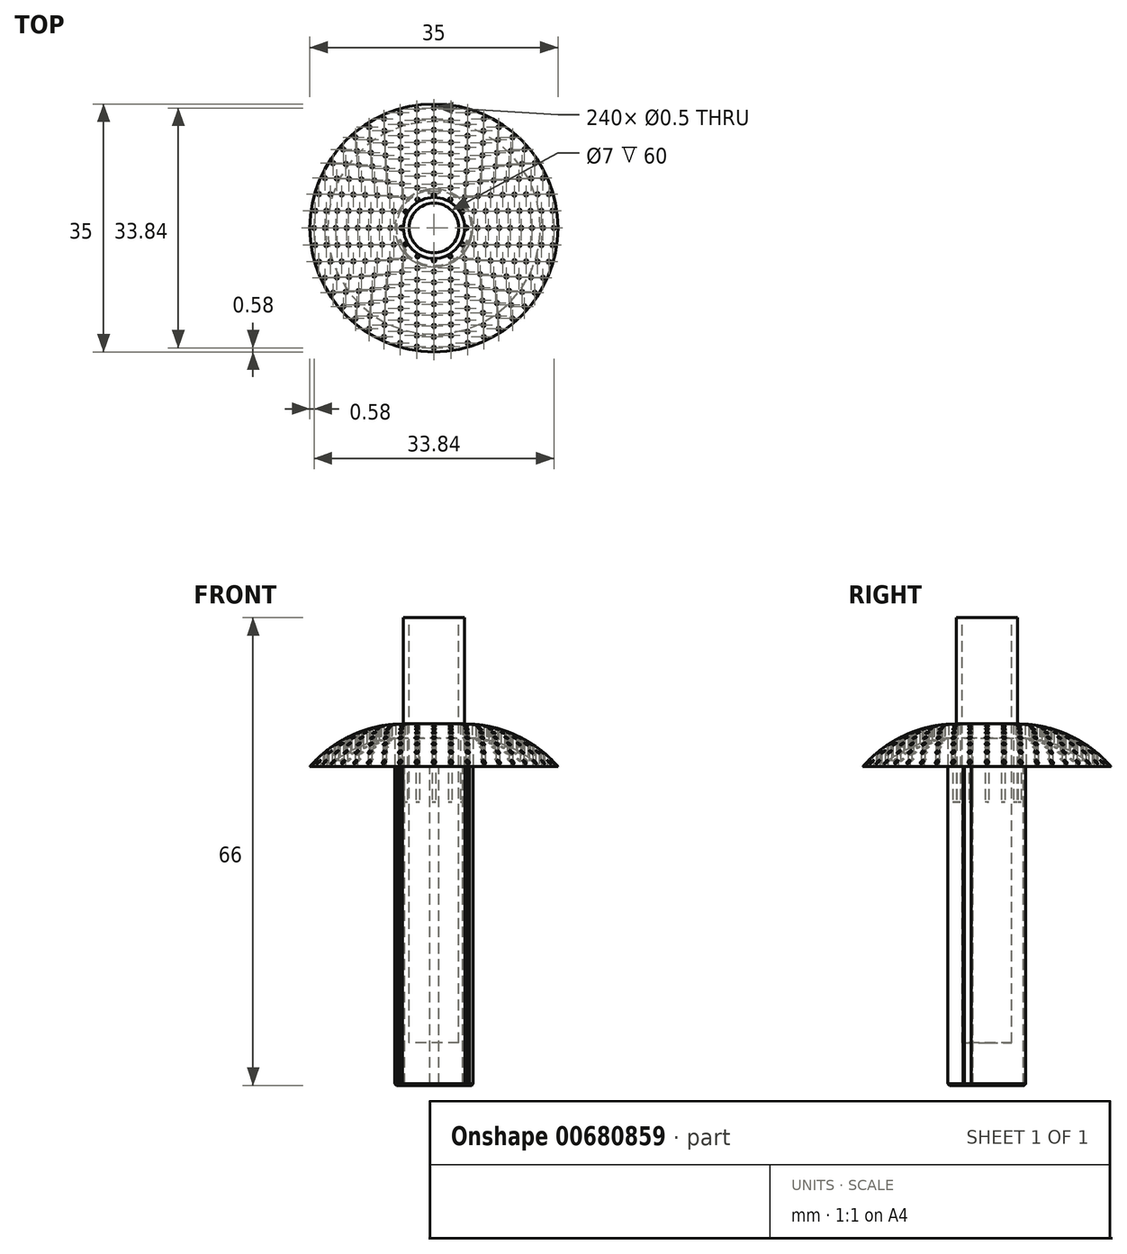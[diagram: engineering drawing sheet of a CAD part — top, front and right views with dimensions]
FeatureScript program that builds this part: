
annotation { "Feature Type Name" : "Feature", "Feature Type Description" : "" }
export const myFeature = defineFeature(function(context is Context, id is Id, definition is map)
    precondition{}
    {
        {
            var Q0;
            Q0=qCreatedBy(makeId("Top.planeOp"),FACE);
            var sketch = newSketch(context, id + "F0", { "sketchPlane" : qUnion([Q0])});
            skCircle(sketch, "E0", {"center": v(0, 0) * mm, "radius": 5.5 * mm});
            skSolve(sketch);
        }
        {
            var Q0;
            Q0=makeQuery(id+"F0.imprint","IMPRINT",FACE,{"disambiguationData":[TD([[makeQuery(id+"F0.imprint","IMPRINT",EDGE,{"derivedFrom":sQuery(id+"F0.wireOp",EDGE,"E0")}),1.0]])]});
            var Q1;
            Q1=sQuery(id+"F0.wireOp",EDGE,"E0");
            extrude(context, id + "F1", {"entities" : qUnion([Q0]), "surfaceEntities" : qUnion([Q1]), "depth" : 45 * mm, "offsetDistance" : 25 * mm});
        }
        {
            var Q0;
            Q0=makeQuery(id+"F1.opExtrude","CAP_FACE",FACE,{"disambiguationData":[OSD([sQuery(id+"F0.wireOp",EDGE,"E0")])],"isStart":false});
            var sketch = newSketch(context, id + "F2", { "sketchPlane" : qUnion([Q0])});
            skLineSegment(sketch, "E1.bottom", {"start": v(-0.6, 7.22) * mm, "end": v(0.71, 7.22) * mm});
            skLineSegment(sketch, "E1.top", {"start": v(-0.6, 5.12) * mm, "end": v(0.71, 5.12) * mm});
            skLineSegment(sketch, "E1.left", {"start": v(-0.6, 7.22) * mm, "end": v(-0.6, 5.12) * mm});
            skLineSegment(sketch, "E1.right", {"start": v(0.71, 7.22) * mm, "end": v(0.71, 5.12) * mm});
            skLineSegment(sketch, "E2.1.0", {"start": v(-6.6, -2.99) * mm, "end": v(-4.8, -1.94) * mm});
            skLineSegment(sketch, "E2.1.1", {"start": v(-4.13, -3.08) * mm, "end": v(-4.8, -1.94) * mm});
            skLineSegment(sketch, "E2.1.2", {"start": v(-5.95, -4.13) * mm, "end": v(-4.13, -3.08) * mm});
            skLineSegment(sketch, "E2.1.3", {"start": v(-5.95, -4.13) * mm, "end": v(-6.6, -2.99) * mm});
            skLineSegment(sketch, "E2.2.0", {"start": v(5.9, -4.23) * mm, "end": v(4.08, -3.18) * mm});
            skLineSegment(sketch, "E2.2.1", {"start": v(4.73, -2.04) * mm, "end": v(4.08, -3.18) * mm});
            skLineSegment(sketch, "E2.2.2", {"start": v(6.55, -3.09) * mm, "end": v(4.73, -2.04) * mm});
            skLineSegment(sketch, "E2.2.3", {"start": v(6.55, -3.09) * mm, "end": v(5.9, -4.23) * mm});
            skPoint(sketch, "E2.center", {"position": v(0, 0) * mm});
            skSolve(sketch);
        }
        {
            var Q0;
            Q0 = qSketchRegion(id + "F2", true);
            extrude(context, id + "F3", {"entities" : qUnion([Q0]), "operationType" : NewBodyOperationType.REMOVE, "oppositeDirection" : true, "depth" : 50 * mm, "offsetDistance" : 25 * mm});
        }
        {
            var Q0;
            Q0=makeQuery(id+"F1.opExtrude","CAP_FACE",FACE,{"disambiguationData":[OSD([sQuery(id+"F0.wireOp",EDGE,"E0")])],"isStart":false});
            var sketch = newSketch(context, id + "F4", { "sketchPlane" : qUnion([Q0])});
            skCircle(sketch, "E3", {"center": v(0, 0) * mm, "radius": 17.5 * mm});
            skSolve(sketch);
        }
        {
            var Q0;
            Q0 = qSketchRegion(id + "F4", true);
            extrude(context, id + "F5", {"entities" : qUnion([Q0]), "operationType" : NewBodyOperationType.ADD, "depth" : 6 * mm, "offsetDistance" : 25 * mm});
        }
        {
            var Q0;
            Q0=makeQuery(id+"F5.opExtrude","CAP_EDGE",EDGE,{"disambiguationData":[OSD([sQuery(id+"F4.wireOp",EDGE,"E3")])],"isStart":false});
            fillet(context, id + "F6", {"entities" : qUnion([Q0]), "radius" : 17.5 * mm, "tangentPropagation" : true, "allowEdgeOverflow" : false});
        }
        {
            var Q0;
            Q0=makeQuery(id+"F5.opExtrude","CAP_FACE",FACE,{"disambiguationData":[OSD([sQuery(id+"F4.wireOp",EDGE,"E3")])],"isStart":false});
            var sketch = newSketch(context, id + "F7", { "sketchPlane" : qUnion([Q0])});
            skCircle(sketch, "E4", {"center": v(0, 0) * mm, "radius": 3.5 * mm});
            skSolve(sketch);
        }
        {
            var Q0;
            Q0 = qSketchRegion(id + "F7", true);
            extrude(context, id + "F8", {"entities" : qUnion([Q0]), "operationType" : NewBodyOperationType.REMOVE, "oppositeDirection" : true, "depth" : 45 * mm, "offsetDistance" : 25 * mm});
        }
        {
            var Q0;
            Q0=makeQuery(id+"F3.boolean.opBoolean","INTERSECT",EDGE,{"derivedFrom":[makeQuery(id+"F1.opExtrude","CAP_FACE",FACE,{"disambiguationData":[OSD([sQuery(id+"F0.wireOp",EDGE,"E0")])],"isStart":true}),makeQuery(id+"F3.opExtrude","SWEPT_FACE",FACE,{"disambiguationData":[OSD([sQuery(id+"F2.wireOp",EDGE,"E2.2.1")])]})]});
            var Q1;
            Q1=makeQuery(id+"F1.opExtrude","CAP_FACE",FACE,{"disambiguationData":[OSD([sQuery(id+"F0.wireOp",EDGE,"E0")])],"isStart":true});
            chamfer(context, id + "F9", {"entities" : qUnion([Q0, Q1]), "width" : 0.2 * mm, "tangentPropagation" : true});
        }
        {
            var Q0;
            Q0=qCreatedBy(makeId("Top.planeOp"),FACE);
            cPlane(context, id + "F10", {"entities" : qUnion([Q0]), "cplaneType" : CPlaneType.OFFSET, "offset" : 40 * mm, "width" : 150 * mm, "height" : 150 * mm});
        }
        {
            var Q0;
            Q0=qCreatedBy(id+"F10.planeOp",FACE);
            var sketch = newSketch(context, id + "F11", { "sketchPlane" : qUnion([Q0])});
            skCircle(sketch, "E5", {"center": v(0, 4.6) * mm, "radius": 0.25 * mm});
            skLineSegment(sketch, "E6", {"start": v(0, 0) * mm, "end": v(0, 6.89) * mm});
            skCircle(sketch, "E7.1.0.0", {"center": v(0, 6.14) * mm, "radius": 0.25 * mm});
            skCircle(sketch, "E7.2.0.0", {"center": v(0, 7.68) * mm, "radius": 0.25 * mm});
            skCircle(sketch, "E7.3.0.0", {"center": v(0, 9.22) * mm, "radius": 0.25 * mm});
            skCircle(sketch, "E7.4.0.0", {"center": v(0, 10.76) * mm, "radius": 0.25 * mm});
            skCircle(sketch, "E7.5.0.0", {"center": v(0, 12.3) * mm, "radius": 0.25 * mm});
            skLineSegment(sketch, "E7.direction1", {"start": v(0, 4.6) * mm, "end": v(0, 6.14) * mm, "construction": true});
            skCircle(sketch, "E8.1.0", {"center": v(-2.3, 3.98) * mm, "radius": 0.25 * mm});
            skCircle(sketch, "E8.2.0", {"center": v(-3.98, 2.3) * mm, "radius": 0.25 * mm});
            skCircle(sketch, "E8.3.0", {"center": v(-4.6, 0) * mm, "radius": 0.25 * mm});
            skCircle(sketch, "E8.4.0", {"center": v(-3.98, -2.3) * mm, "radius": 0.25 * mm});
            skCircle(sketch, "E8.5.0", {"center": v(-2.3, -3.98) * mm, "radius": 0.25 * mm});
            skCircle(sketch, "E8.6.0", {"center": v(0, -4.6) * mm, "radius": 0.25 * mm});
            skCircle(sketch, "E8.7.0", {"center": v(2.3, -3.98) * mm, "radius": 0.25 * mm});
            skCircle(sketch, "E8.8.0", {"center": v(3.98, -2.3) * mm, "radius": 0.25 * mm});
            skCircle(sketch, "E8.9.0", {"center": v(4.6, 0) * mm, "radius": 0.25 * mm});
            skCircle(sketch, "E8.10.0", {"center": v(3.98, 2.3) * mm, "radius": 0.25 * mm});
            skCircle(sketch, "E8.11.0", {"center": v(2.3, 3.98) * mm, "radius": 0.25 * mm});
            skPoint(sketch, "E8.center", {"position": v(0, 0) * mm});
            skCircle(sketch, "E9.1.0", {"center": v(-2.35, 5.67) * mm, "radius": 0.25 * mm});
            skCircle(sketch, "E9.2.0", {"center": v(-4.34, 4.34) * mm, "radius": 0.25 * mm});
            skCircle(sketch, "E9.3.0", {"center": v(-5.67, 2.35) * mm, "radius": 0.25 * mm});
            skCircle(sketch, "E9.4.0", {"center": v(-6.14, 0) * mm, "radius": 0.25 * mm});
            skCircle(sketch, "E9.5.0", {"center": v(-5.67, -2.35) * mm, "radius": 0.25 * mm});
            skCircle(sketch, "E9.6.0", {"center": v(-4.34, -4.34) * mm, "radius": 0.25 * mm});
            skCircle(sketch, "E9.7.0", {"center": v(-2.35, -5.67) * mm, "radius": 0.25 * mm});
            skCircle(sketch, "E9.8.0", {"center": v(0, -6.14) * mm, "radius": 0.25 * mm});
            skCircle(sketch, "E9.9.0", {"center": v(2.35, -5.67) * mm, "radius": 0.25 * mm});
            skCircle(sketch, "E9.10.0", {"center": v(4.34, -4.34) * mm, "radius": 0.25 * mm});
            skCircle(sketch, "E9.11.0", {"center": v(5.67, -2.35) * mm, "radius": 0.25 * mm});
            skCircle(sketch, "E9.12.0", {"center": v(6.14, 0) * mm, "radius": 0.25 * mm});
            skCircle(sketch, "E9.13.0", {"center": v(5.67, 2.35) * mm, "radius": 0.25 * mm});
            skCircle(sketch, "E9.14.0", {"center": v(4.34, 4.34) * mm, "radius": 0.25 * mm});
            skCircle(sketch, "E9.15.0", {"center": v(2.35, 5.67) * mm, "radius": 0.25 * mm});
            skCircle(sketch, "E10.1.0", {"center": v(-2.37, 7.3) * mm, "radius": 0.25 * mm});
            skCircle(sketch, "E10.2.0", {"center": v(-4.51, 6.21) * mm, "radius": 0.25 * mm});
            skCircle(sketch, "E10.3.0", {"center": v(-6.21, 4.51) * mm, "radius": 0.25 * mm});
            skCircle(sketch, "E10.4.0", {"center": v(-7.3, 2.37) * mm, "radius": 0.25 * mm});
            skCircle(sketch, "E10.5.0", {"center": v(-7.68, 0) * mm, "radius": 0.25 * mm});
            skCircle(sketch, "E10.6.0", {"center": v(-7.3, -2.37) * mm, "radius": 0.25 * mm});
            skCircle(sketch, "E10.7.0", {"center": v(-6.21, -4.51) * mm, "radius": 0.25 * mm});
            skCircle(sketch, "E10.8.0", {"center": v(-4.51, -6.21) * mm, "radius": 0.25 * mm});
            skCircle(sketch, "E10.9.0", {"center": v(-2.37, -7.3) * mm, "radius": 0.25 * mm});
            skCircle(sketch, "E10.10.0", {"center": v(0, -7.68) * mm, "radius": 0.25 * mm});
            skCircle(sketch, "E10.11.0", {"center": v(2.37, -7.3) * mm, "radius": 0.25 * mm});
            skCircle(sketch, "E10.12.0", {"center": v(4.51, -6.21) * mm, "radius": 0.25 * mm});
            skCircle(sketch, "E10.13.0", {"center": v(6.21, -4.51) * mm, "radius": 0.25 * mm});
            skCircle(sketch, "E10.14.0", {"center": v(7.3, -2.37) * mm, "radius": 0.25 * mm});
            skCircle(sketch, "E10.15.0", {"center": v(7.68, 0) * mm, "radius": 0.25 * mm});
            skCircle(sketch, "E10.16.0", {"center": v(7.3, 2.37) * mm, "radius": 0.25 * mm});
            skCircle(sketch, "E10.17.0", {"center": v(6.21, 4.51) * mm, "radius": 0.25 * mm});
            skCircle(sketch, "E10.18.0", {"center": v(4.51, 6.21) * mm, "radius": 0.25 * mm});
            skCircle(sketch, "E10.19.0", {"center": v(2.37, 7.3) * mm, "radius": 0.25 * mm});
            skCircle(sketch, "E11.1.0", {"center": v(-2.39, 8.9) * mm, "radius": 0.25 * mm});
            skCircle(sketch, "E11.2.0", {"center": v(-4.6, 7.98) * mm, "radius": 0.25 * mm});
            skCircle(sketch, "E11.3.0", {"center": v(-6.52, 6.52) * mm, "radius": 0.25 * mm});
            skCircle(sketch, "E11.4.0", {"center": v(-7.98, 4.6) * mm, "radius": 0.25 * mm});
            skCircle(sketch, "E11.5.0", {"center": v(-8.9, 2.39) * mm, "radius": 0.25 * mm});
            skCircle(sketch, "E11.6.0", {"center": v(-9.22, 0) * mm, "radius": 0.25 * mm});
            skCircle(sketch, "E11.7.0", {"center": v(-8.9, -2.39) * mm, "radius": 0.25 * mm});
            skCircle(sketch, "E11.8.0", {"center": v(-7.98, -4.6) * mm, "radius": 0.25 * mm});
            skCircle(sketch, "E11.9.0", {"center": v(-6.52, -6.52) * mm, "radius": 0.25 * mm});
            skCircle(sketch, "E11.10.0", {"center": v(-4.61, -7.98) * mm, "radius": 0.25 * mm});
            skCircle(sketch, "E11.11.0", {"center": v(-2.39, -8.9) * mm, "radius": 0.25 * mm});
            skCircle(sketch, "E11.12.0", {"center": v(0, -9.22) * mm, "radius": 0.25 * mm});
            skCircle(sketch, "E11.13.0", {"center": v(2.39, -8.9) * mm, "radius": 0.25 * mm});
            skCircle(sketch, "E11.14.0", {"center": v(4.6, -7.98) * mm, "radius": 0.25 * mm});
            skCircle(sketch, "E11.15.0", {"center": v(6.52, -6.52) * mm, "radius": 0.25 * mm});
            skCircle(sketch, "E11.16.0", {"center": v(7.98, -4.61) * mm, "radius": 0.25 * mm});
            skCircle(sketch, "E11.17.0", {"center": v(8.9, -2.39) * mm, "radius": 0.25 * mm});
            skCircle(sketch, "E11.18.0", {"center": v(9.22, 0) * mm, "radius": 0.25 * mm});
            skCircle(sketch, "E11.19.0", {"center": v(8.9, 2.39) * mm, "radius": 0.25 * mm});
            skCircle(sketch, "E11.20.0", {"center": v(7.98, 4.6) * mm, "radius": 0.25 * mm});
            skCircle(sketch, "E11.21.0", {"center": v(6.52, 6.52) * mm, "radius": 0.25 * mm});
            skCircle(sketch, "E11.22.0", {"center": v(4.61, 7.98) * mm, "radius": 0.25 * mm});
            skCircle(sketch, "E11.23.0", {"center": v(2.39, 8.9) * mm, "radius": 0.25 * mm});
            skCircle(sketch, "E12.1.0", {"center": v(-2.4, 10.5) * mm, "radius": 0.25 * mm});
            skCircle(sketch, "E12.2.0", {"center": v(-4.67, 9.7) * mm, "radius": 0.25 * mm});
            skCircle(sketch, "E12.3.0", {"center": v(-6.7, 8.41) * mm, "radius": 0.25 * mm});
            skCircle(sketch, "E12.4.0", {"center": v(-8.41, 6.7) * mm, "radius": 0.25 * mm});
            skCircle(sketch, "E12.5.0", {"center": v(-9.7, 4.67) * mm, "radius": 0.25 * mm});
            skCircle(sketch, "E12.6.0", {"center": v(-10.5, 2.4) * mm, "radius": 0.25 * mm});
            skCircle(sketch, "E12.7.0", {"center": v(-10.76, 0) * mm, "radius": 0.25 * mm});
            skCircle(sketch, "E12.8.0", {"center": v(-10.5, -2.4) * mm, "radius": 0.25 * mm});
            skCircle(sketch, "E12.9.0", {"center": v(-9.7, -4.67) * mm, "radius": 0.25 * mm});
            skCircle(sketch, "E12.10.0", {"center": v(-8.41, -6.7) * mm, "radius": 0.25 * mm});
            skCircle(sketch, "E12.11.0", {"center": v(-6.7, -8.41) * mm, "radius": 0.25 * mm});
            skCircle(sketch, "E12.12.0", {"center": v(-4.67, -9.7) * mm, "radius": 0.25 * mm});
            skCircle(sketch, "E12.13.0", {"center": v(-2.4, -10.5) * mm, "radius": 0.25 * mm});
            skCircle(sketch, "E12.14.0", {"center": v(0, -10.76) * mm, "radius": 0.25 * mm});
            skCircle(sketch, "E12.15.0", {"center": v(2.4, -10.5) * mm, "radius": 0.25 * mm});
            skCircle(sketch, "E12.16.0", {"center": v(4.67, -9.7) * mm, "radius": 0.25 * mm});
            skCircle(sketch, "E12.17.0", {"center": v(6.7, -8.41) * mm, "radius": 0.25 * mm});
            skCircle(sketch, "E12.18.0", {"center": v(8.41, -6.7) * mm, "radius": 0.25 * mm});
            skCircle(sketch, "E12.19.0", {"center": v(9.7, -4.67) * mm, "radius": 0.25 * mm});
            skCircle(sketch, "E12.20.0", {"center": v(10.5, -2.4) * mm, "radius": 0.25 * mm});
            skCircle(sketch, "E12.21.0", {"center": v(10.76, 0) * mm, "radius": 0.25 * mm});
            skCircle(sketch, "E12.22.0", {"center": v(10.5, 2.4) * mm, "radius": 0.25 * mm});
            skCircle(sketch, "E12.23.0", {"center": v(9.7, 4.67) * mm, "radius": 0.25 * mm});
            skCircle(sketch, "E12.24.0", {"center": v(8.41, 6.7) * mm, "radius": 0.25 * mm});
            skCircle(sketch, "E12.25.0", {"center": v(6.7, 8.41) * mm, "radius": 0.25 * mm});
            skCircle(sketch, "E12.26.0", {"center": v(4.67, 9.7) * mm, "radius": 0.25 * mm});
            skCircle(sketch, "E12.27.0", {"center": v(2.4, 10.5) * mm, "radius": 0.25 * mm});
            skCircle(sketch, "E13.1.0", {"center": v(-2.4, 12.06) * mm, "radius": 0.25 * mm});
            skCircle(sketch, "E13.2.0", {"center": v(-4.7, 11.36) * mm, "radius": 0.25 * mm});
            skCircle(sketch, "E13.3.0", {"center": v(-6.83, 10.23) * mm, "radius": 0.25 * mm});
            skCircle(sketch, "E13.4.0", {"center": v(-8.7, 8.7) * mm, "radius": 0.25 * mm});
            skCircle(sketch, "E13.5.0", {"center": v(-10.23, 6.83) * mm, "radius": 0.25 * mm});
            skCircle(sketch, "E13.6.0", {"center": v(-11.36, 4.7) * mm, "radius": 0.25 * mm});
            skCircle(sketch, "E13.7.0", {"center": v(-12.06, 2.4) * mm, "radius": 0.25 * mm});
            skCircle(sketch, "E13.8.0", {"center": v(-12.3, 0) * mm, "radius": 0.25 * mm});
            skCircle(sketch, "E13.9.0", {"center": v(-12.06, -2.4) * mm, "radius": 0.25 * mm});
            skCircle(sketch, "E13.10.0", {"center": v(-11.36, -4.7) * mm, "radius": 0.25 * mm});
            skCircle(sketch, "E13.11.0", {"center": v(-10.23, -6.83) * mm, "radius": 0.25 * mm});
            skCircle(sketch, "E13.12.0", {"center": v(-8.7, -8.7) * mm, "radius": 0.25 * mm});
            skCircle(sketch, "E13.13.0", {"center": v(-6.83, -10.23) * mm, "radius": 0.25 * mm});
            skCircle(sketch, "E13.14.0", {"center": v(-4.7, -11.36) * mm, "radius": 0.25 * mm});
            skCircle(sketch, "E13.15.0", {"center": v(-2.4, -12.06) * mm, "radius": 0.25 * mm});
            skCircle(sketch, "E13.16.0", {"center": v(0, -12.3) * mm, "radius": 0.25 * mm});
            skCircle(sketch, "E13.17.0", {"center": v(2.4, -12.06) * mm, "radius": 0.25 * mm});
            skCircle(sketch, "E13.18.0", {"center": v(4.7, -11.36) * mm, "radius": 0.25 * mm});
            skCircle(sketch, "E13.19.0", {"center": v(6.83, -10.23) * mm, "radius": 0.25 * mm});
            skCircle(sketch, "E13.20.0", {"center": v(8.7, -8.7) * mm, "radius": 0.25 * mm});
            skCircle(sketch, "E13.21.0", {"center": v(10.23, -6.83) * mm, "radius": 0.25 * mm});
            skCircle(sketch, "E13.22.0", {"center": v(11.36, -4.7) * mm, "radius": 0.25 * mm});
            skCircle(sketch, "E13.23.0", {"center": v(12.06, -2.4) * mm, "radius": 0.25 * mm});
            skCircle(sketch, "E13.24.0", {"center": v(12.3, 0) * mm, "radius": 0.25 * mm});
            skCircle(sketch, "E13.25.0", {"center": v(12.06, 2.4) * mm, "radius": 0.25 * mm});
            skCircle(sketch, "E13.26.0", {"center": v(11.36, 4.7) * mm, "radius": 0.25 * mm});
            skCircle(sketch, "E13.27.0", {"center": v(10.23, 6.83) * mm, "radius": 0.25 * mm});
            skCircle(sketch, "E13.28.0", {"center": v(8.7, 8.7) * mm, "radius": 0.25 * mm});
            skCircle(sketch, "E13.29.0", {"center": v(6.83, 10.23) * mm, "radius": 0.25 * mm});
            skCircle(sketch, "E13.30.0", {"center": v(4.7, 11.36) * mm, "radius": 0.25 * mm});
            skCircle(sketch, "E13.31.0", {"center": v(2.4, 12.06) * mm, "radius": 0.25 * mm});
            skCircle(sketch, "E14.0.6.0", {"center": v(0, 13.84) * mm, "radius": 0.25 * mm});
            skCircle(sketch, "E14.0.7.0", {"center": v(0, 15.38) * mm, "radius": 0.25 * mm});
            skCircle(sketch, "E15.0.8.0", {"center": v(0, 16.92) * mm, "radius": 0.25 * mm});
            skCircle(sketch, "E16.1.0", {"center": v(-2.4, 13.63) * mm, "radius": 0.25 * mm});
            skCircle(sketch, "E16.2.0", {"center": v(-4.73, 13) * mm, "radius": 0.25 * mm});
            skCircle(sketch, "E16.3.0", {"center": v(-6.92, 11.99) * mm, "radius": 0.25 * mm});
            skCircle(sketch, "E16.4.0", {"center": v(-8.9, 10.6) * mm, "radius": 0.25 * mm});
            skCircle(sketch, "E16.5.0", {"center": v(-10.6, 8.9) * mm, "radius": 0.25 * mm});
            skCircle(sketch, "E16.6.0", {"center": v(-11.99, 6.92) * mm, "radius": 0.25 * mm});
            skCircle(sketch, "E16.7.0", {"center": v(-13, 4.73) * mm, "radius": 0.25 * mm});
            skCircle(sketch, "E16.8.0", {"center": v(-13.63, 2.4) * mm, "radius": 0.25 * mm});
            skCircle(sketch, "E16.9.0", {"center": v(-13.84, 0) * mm, "radius": 0.25 * mm});
            skCircle(sketch, "E16.10.0", {"center": v(-13.63, -2.4) * mm, "radius": 0.25 * mm});
            skCircle(sketch, "E16.11.0", {"center": v(-13, -4.73) * mm, "radius": 0.25 * mm});
            skCircle(sketch, "E16.12.0", {"center": v(-11.99, -6.92) * mm, "radius": 0.25 * mm});
            skCircle(sketch, "E16.13.0", {"center": v(-10.6, -8.9) * mm, "radius": 0.25 * mm});
            skCircle(sketch, "E16.14.0", {"center": v(-8.9, -10.6) * mm, "radius": 0.25 * mm});
            skCircle(sketch, "E16.15.0", {"center": v(-6.92, -11.99) * mm, "radius": 0.25 * mm});
            skCircle(sketch, "E16.16.0", {"center": v(-4.73, -13) * mm, "radius": 0.25 * mm});
            skCircle(sketch, "E16.17.0", {"center": v(-2.4, -13.63) * mm, "radius": 0.25 * mm});
            skCircle(sketch, "E16.18.0", {"center": v(0, -13.84) * mm, "radius": 0.25 * mm});
            skCircle(sketch, "E16.19.0", {"center": v(2.4, -13.63) * mm, "radius": 0.25 * mm});
            skCircle(sketch, "E16.20.0", {"center": v(4.73, -13) * mm, "radius": 0.25 * mm});
            skCircle(sketch, "E16.21.0", {"center": v(6.92, -11.99) * mm, "radius": 0.25 * mm});
            skCircle(sketch, "E16.22.0", {"center": v(8.9, -10.6) * mm, "radius": 0.25 * mm});
            skCircle(sketch, "E16.23.0", {"center": v(10.6, -8.9) * mm, "radius": 0.25 * mm});
            skCircle(sketch, "E16.24.0", {"center": v(11.99, -6.92) * mm, "radius": 0.25 * mm});
            skCircle(sketch, "E16.25.0", {"center": v(13, -4.73) * mm, "radius": 0.25 * mm});
            skCircle(sketch, "E16.26.0", {"center": v(13.63, -2.4) * mm, "radius": 0.25 * mm});
            skCircle(sketch, "E16.27.0", {"center": v(13.84, 0) * mm, "radius": 0.25 * mm});
            skCircle(sketch, "E16.28.0", {"center": v(13.63, 2.4) * mm, "radius": 0.25 * mm});
            skCircle(sketch, "E16.29.0", {"center": v(13, 4.73) * mm, "radius": 0.25 * mm});
            skCircle(sketch, "E16.30.0", {"center": v(11.99, 6.92) * mm, "radius": 0.25 * mm});
            skCircle(sketch, "E16.31.0", {"center": v(10.6, 8.9) * mm, "radius": 0.25 * mm});
            skCircle(sketch, "E16.32.0", {"center": v(8.9, 10.6) * mm, "radius": 0.25 * mm});
            skCircle(sketch, "E16.33.0", {"center": v(6.92, 11.99) * mm, "radius": 0.25 * mm});
            skCircle(sketch, "E16.34.0", {"center": v(4.73, 13) * mm, "radius": 0.25 * mm});
            skCircle(sketch, "E16.35.0", {"center": v(2.4, 13.63) * mm, "radius": 0.25 * mm});
            skCircle(sketch, "E17.1.0", {"center": v(-2.4, 15.2) * mm, "radius": 0.25 * mm});
            skCircle(sketch, "E17.2.0", {"center": v(-4.75, 14.63) * mm, "radius": 0.25 * mm});
            skCircle(sketch, "E17.3.0", {"center": v(-6.98, 13.7) * mm, "radius": 0.25 * mm});
            skCircle(sketch, "E17.4.0", {"center": v(-9.04, 12.44) * mm, "radius": 0.25 * mm});
            skCircle(sketch, "E17.5.0", {"center": v(-10.88, 10.88) * mm, "radius": 0.25 * mm});
            skCircle(sketch, "E17.6.0", {"center": v(-12.44, 9.04) * mm, "radius": 0.25 * mm});
            skCircle(sketch, "E17.7.0", {"center": v(-13.7, 6.98) * mm, "radius": 0.25 * mm});
            skCircle(sketch, "E17.8.0", {"center": v(-14.63, 4.75) * mm, "radius": 0.25 * mm});
            skCircle(sketch, "E17.9.0", {"center": v(-15.2, 2.4) * mm, "radius": 0.25 * mm});
            skCircle(sketch, "E17.10.0", {"center": v(-15.38, 0) * mm, "radius": 0.25 * mm});
            skCircle(sketch, "E17.11.0", {"center": v(-15.2, -2.4) * mm, "radius": 0.25 * mm});
            skCircle(sketch, "E17.12.0", {"center": v(-14.63, -4.75) * mm, "radius": 0.25 * mm});
            skCircle(sketch, "E17.13.0", {"center": v(-13.7, -6.98) * mm, "radius": 0.25 * mm});
            skCircle(sketch, "E17.14.0", {"center": v(-12.44, -9.04) * mm, "radius": 0.25 * mm});
            skCircle(sketch, "E17.15.0", {"center": v(-10.88, -10.88) * mm, "radius": 0.25 * mm});
            skCircle(sketch, "E17.16.0", {"center": v(-9.04, -12.44) * mm, "radius": 0.25 * mm});
            skCircle(sketch, "E17.17.0", {"center": v(-6.98, -13.7) * mm, "radius": 0.25 * mm});
            skCircle(sketch, "E17.18.0", {"center": v(-4.75, -14.63) * mm, "radius": 0.25 * mm});
            skCircle(sketch, "E17.19.0", {"center": v(-2.4, -15.2) * mm, "radius": 0.25 * mm});
            skCircle(sketch, "E17.20.0", {"center": v(0, -15.38) * mm, "radius": 0.25 * mm});
            skCircle(sketch, "E17.21.0", {"center": v(2.4, -15.2) * mm, "radius": 0.25 * mm});
            skCircle(sketch, "E17.22.0", {"center": v(4.75, -14.63) * mm, "radius": 0.25 * mm});
            skCircle(sketch, "E17.23.0", {"center": v(6.98, -13.7) * mm, "radius": 0.25 * mm});
            skCircle(sketch, "E17.24.0", {"center": v(9.04, -12.44) * mm, "radius": 0.25 * mm});
            skCircle(sketch, "E17.25.0", {"center": v(10.88, -10.88) * mm, "radius": 0.25 * mm});
            skCircle(sketch, "E17.26.0", {"center": v(12.44, -9.04) * mm, "radius": 0.25 * mm});
            skCircle(sketch, "E17.27.0", {"center": v(13.7, -6.98) * mm, "radius": 0.25 * mm});
            skCircle(sketch, "E17.28.0", {"center": v(14.63, -4.75) * mm, "radius": 0.25 * mm});
            skCircle(sketch, "E17.29.0", {"center": v(15.2, -2.4) * mm, "radius": 0.25 * mm});
            skCircle(sketch, "E17.30.0", {"center": v(15.38, 0) * mm, "radius": 0.25 * mm});
            skCircle(sketch, "E17.31.0", {"center": v(15.2, 2.4) * mm, "radius": 0.25 * mm});
            skCircle(sketch, "E17.32.0", {"center": v(14.63, 4.75) * mm, "radius": 0.25 * mm});
            skCircle(sketch, "E17.33.0", {"center": v(13.7, 6.98) * mm, "radius": 0.25 * mm});
            skCircle(sketch, "E17.34.0", {"center": v(12.44, 9.04) * mm, "radius": 0.25 * mm});
            skCircle(sketch, "E17.35.0", {"center": v(10.88, 10.88) * mm, "radius": 0.25 * mm});
            skCircle(sketch, "E17.36.0", {"center": v(9.04, 12.44) * mm, "radius": 0.25 * mm});
            skCircle(sketch, "E17.37.0", {"center": v(6.98, 13.7) * mm, "radius": 0.25 * mm});
            skCircle(sketch, "E17.38.0", {"center": v(4.75, 14.63) * mm, "radius": 0.25 * mm});
            skCircle(sketch, "E17.39.0", {"center": v(2.4, 15.2) * mm, "radius": 0.25 * mm});
            skCircle(sketch, "E18.1.0", {"center": v(-2.4, 16.75) * mm, "radius": 0.25 * mm});
            skCircle(sketch, "E18.2.0", {"center": v(-4.77, 16.23) * mm, "radius": 0.25 * mm});
            skCircle(sketch, "E18.3.0", {"center": v(-7.03, 15.4) * mm, "radius": 0.25 * mm});
            skCircle(sketch, "E18.4.0", {"center": v(-9.15, 14.23) * mm, "radius": 0.25 * mm});
            skCircle(sketch, "E18.5.0", {"center": v(-11.08, 12.79) * mm, "radius": 0.25 * mm});
            skCircle(sketch, "E18.6.0", {"center": v(-12.79, 11.08) * mm, "radius": 0.25 * mm});
            skCircle(sketch, "E18.7.0", {"center": v(-14.23, 9.15) * mm, "radius": 0.25 * mm});
            skCircle(sketch, "E18.8.0", {"center": v(-15.4, 7.03) * mm, "radius": 0.25 * mm});
            skCircle(sketch, "E18.9.0", {"center": v(-16.23, 4.77) * mm, "radius": 0.25 * mm});
            skCircle(sketch, "E18.10.0", {"center": v(-16.75, 2.4) * mm, "radius": 0.25 * mm});
            skCircle(sketch, "E18.11.0", {"center": v(-16.92, 0) * mm, "radius": 0.25 * mm});
            skCircle(sketch, "E18.12.0", {"center": v(-16.75, -2.4) * mm, "radius": 0.25 * mm});
            skCircle(sketch, "E18.13.0", {"center": v(-16.23, -4.77) * mm, "radius": 0.25 * mm});
            skCircle(sketch, "E18.14.0", {"center": v(-15.4, -7.03) * mm, "radius": 0.25 * mm});
            skCircle(sketch, "E18.15.0", {"center": v(-14.23, -9.15) * mm, "radius": 0.25 * mm});
            skCircle(sketch, "E18.16.0", {"center": v(-12.79, -11.08) * mm, "radius": 0.25 * mm});
            skCircle(sketch, "E18.17.0", {"center": v(-11.08, -12.79) * mm, "radius": 0.25 * mm});
            skCircle(sketch, "E18.18.0", {"center": v(-9.15, -14.23) * mm, "radius": 0.25 * mm});
            skCircle(sketch, "E18.19.0", {"center": v(-7.03, -15.4) * mm, "radius": 0.25 * mm});
            skCircle(sketch, "E18.20.0", {"center": v(-4.77, -16.23) * mm, "radius": 0.25 * mm});
            skCircle(sketch, "E18.21.0", {"center": v(-2.4, -16.75) * mm, "radius": 0.25 * mm});
            skCircle(sketch, "E18.22.0", {"center": v(0, -16.92) * mm, "radius": 0.25 * mm});
            skCircle(sketch, "E18.23.0", {"center": v(2.4, -16.75) * mm, "radius": 0.25 * mm});
            skCircle(sketch, "E18.24.0", {"center": v(4.77, -16.23) * mm, "radius": 0.25 * mm});
            skCircle(sketch, "E18.25.0", {"center": v(7.03, -15.4) * mm, "radius": 0.25 * mm});
            skCircle(sketch, "E18.26.0", {"center": v(9.15, -14.23) * mm, "radius": 0.25 * mm});
            skCircle(sketch, "E18.27.0", {"center": v(11.08, -12.79) * mm, "radius": 0.25 * mm});
            skCircle(sketch, "E18.28.0", {"center": v(12.79, -11.08) * mm, "radius": 0.25 * mm});
            skCircle(sketch, "E18.29.0", {"center": v(14.23, -9.15) * mm, "radius": 0.25 * mm});
            skCircle(sketch, "E18.30.0", {"center": v(15.4, -7.03) * mm, "radius": 0.25 * mm});
            skCircle(sketch, "E18.31.0", {"center": v(16.23, -4.77) * mm, "radius": 0.25 * mm});
            skCircle(sketch, "E18.32.0", {"center": v(16.75, -2.4) * mm, "radius": 0.25 * mm});
            skCircle(sketch, "E18.33.0", {"center": v(16.92, 0) * mm, "radius": 0.25 * mm});
            skCircle(sketch, "E18.34.0", {"center": v(16.75, 2.4) * mm, "radius": 0.25 * mm});
            skCircle(sketch, "E18.35.0", {"center": v(16.23, 4.77) * mm, "radius": 0.25 * mm});
            skCircle(sketch, "E18.36.0", {"center": v(15.4, 7.03) * mm, "radius": 0.25 * mm});
            skCircle(sketch, "E18.37.0", {"center": v(14.23, 9.15) * mm, "radius": 0.25 * mm});
            skCircle(sketch, "E18.38.0", {"center": v(12.79, 11.08) * mm, "radius": 0.25 * mm});
            skCircle(sketch, "E18.39.0", {"center": v(11.08, 12.79) * mm, "radius": 0.25 * mm});
            skCircle(sketch, "E18.40.0", {"center": v(9.15, 14.23) * mm, "radius": 0.25 * mm});
            skCircle(sketch, "E18.41.0", {"center": v(7.03, 15.4) * mm, "radius": 0.25 * mm});
            skCircle(sketch, "E18.42.0", {"center": v(4.77, 16.23) * mm, "radius": 0.25 * mm});
            skCircle(sketch, "E18.43.0", {"center": v(2.4, 16.75) * mm, "radius": 0.25 * mm});
            skSolve(sketch);
        }
        {
            var Q0;
            Q0 = qSketchRegion(id + "F11", true);
            extrude(context, id + "F12", {"entities" : qUnion([Q0]), "operationType" : NewBodyOperationType.REMOVE, "depth" : 20.5 * mm, "offsetDistance" : 25 * mm});
        }
        {
            var Q0;
            Q0=qCreatedBy(makeId("Right.planeOp"),FACE);
            var sketch = newSketch(context, id + "F13", { "sketchPlane" : qUnion([Q0])});
            skLineSegment(sketch, "E19", {"start": v(5.5, 45) * mm, "end": v(15, 45) * mm});
            skLineSegment(sketch, "E20", {"start": v(5.5, 45) * mm, "end": v(5.5, 49) * mm});
            skArc(sketch, "E21", {"start": v(15, 45) * mm, "mid": v(10.57, 47.77) * mm, "end": v(5.5, 49) * mm});
            skSolve(sketch);
        }
        {
            var Q0;
            Q0=qCreatedBy(makeId("Right.planeOp"),FACE);
            var sketch = newSketch(context, id + "F14", { "sketchPlane" : qUnion([Q0])});
            skLineSegment(sketch, "E22", {"start": v(0, 0) * mm, "end": v(0, 34.1) * mm});
            skSolve(sketch);
        }
        {
            var Q0;
            Q0 = qSketchRegion(id + "F13", true);
            var Q1;
            Q1=sQuery(id+"F14.wireOp",EDGE,"E22");
            revolve(context, id + "F15", {"operationType" : NewBodyOperationType.REMOVE, "entities" : qUnion([Q0]), "axis" : qUnion([Q1]), "revolveType" : RevolveType.FULL, "oppositeDirection" : true});
        }
        {
            var Q0;
            Q0=makeQuery(id+"F5.opExtrude","CAP_FACE",FACE,{"disambiguationData":[OSD([sQuery(id+"F4.wireOp",EDGE,"E3")])],"isStart":false});
            extrude(context, id + "F16", {"entities" : qUnion([Q0]), "operationType" : NewBodyOperationType.ADD, "depth" : 15 * mm, "offsetDistance" : 25 * mm});
        }
    });
